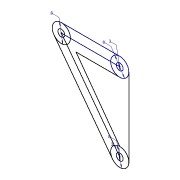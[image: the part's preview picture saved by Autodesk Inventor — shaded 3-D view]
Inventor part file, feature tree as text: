
AUTODESK INVENTOR PART (.ipt)
format: ipt  version: 2018 (Build 220112000, 112)  size: 71,168 bytes
history: native  units: mm
features: sketch x1
ambient origin geometry x8: Origin, YZ Plane, XZ Plane, XY Plane, X Axis, Y Axis, Z Axis, Center Point
feature tree (1):
  sketch  "Sketch1"  dims[d0=8.0mm d1=3.0mm d2=8.0mm d3=3.0mm d4=8.0mm]
